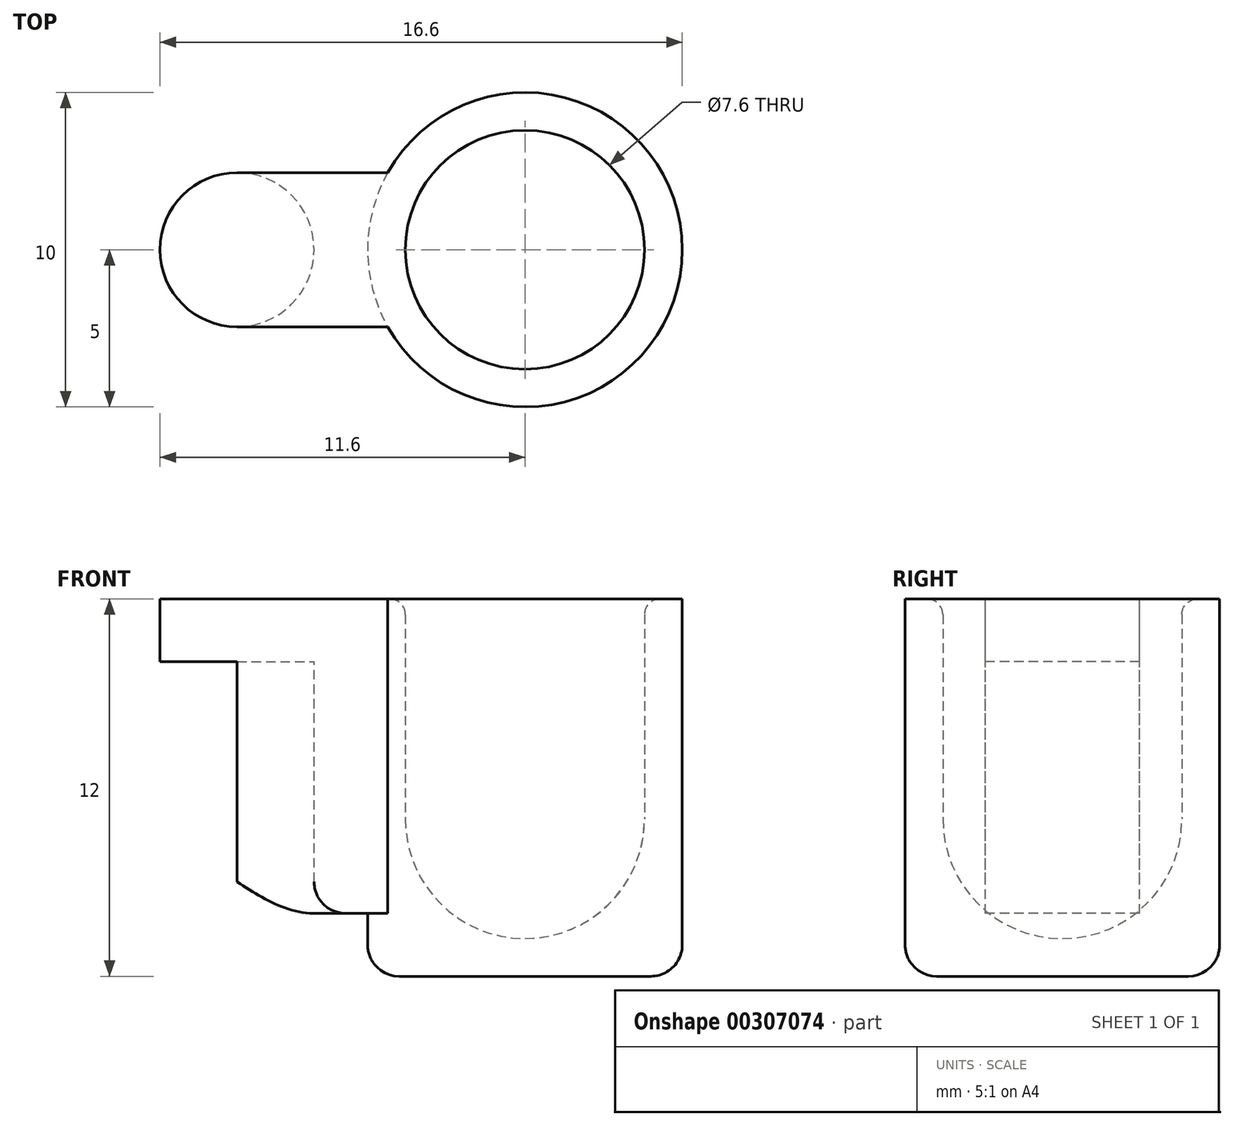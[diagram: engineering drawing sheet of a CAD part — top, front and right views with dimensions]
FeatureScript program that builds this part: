
annotation { "Feature Type Name" : "Feature", "Feature Type Description" : "" }
export const myFeature = defineFeature(function(context is Context, id is Id, definition is map)
    precondition{}
    {
        {
            var Q0;
            Q0=qCreatedBy(makeId("Top.planeOp"),FACE);
            var sketch = newSketch(context, id + "F0", { "sketchPlane" : qUnion([Q0])});
            skCircle(sketch, "E0", {"center": v(0, 0) * mm, "radius": 5 * mm});
            skSolve(sketch);
        }
        {
            var Q0;
            Q0=makeQuery(id+"F0.imprint","IMPRINT",FACE,{"disambiguationData":[TD([[makeQuery(id+"F0.imprint","IMPRINT",EDGE,{"derivedFrom":sQuery(id+"F0.wireOp",EDGE,"E0")}),1.0]])]});
            extrude(context, id + "F1", {"entities" : qUnion([Q0]), "depth" : 12 * mm});
        }
        {
            var Q0;
            Q0=makeQuery(id+"F1.opExtrude","CAP_FACE",FACE,{"disambiguationData":[OSD([sQuery(id+"F0.wireOp",EDGE,"E0")])],"isStart":false});
            shell(context, id + "F2", {"entities" : qUnion([Q0]), "thickness" : 1.2 * mm});
        }
        {
            var Q0;
            Q0=makeQuery(id+"F1.opExtrude","CAP_FACE",FACE,{"disambiguationData":[OSD([sQuery(id+"F0.wireOp",EDGE,"E0")])],"isStart":true});
            var sketch = newSketch(context, id + "F3", { "sketchPlane" : qUnion([Q0])});
            skCircle(sketch, "E1", {"center": v(0, 0) * mm, "radius": 3.5 * mm});
            skSolve(sketch);
        }
        {
            var Q0;
            Q0=makeQuery(id+"F1.opExtrude","CAP_FACE",FACE,{"disambiguationData":[OSD([sQuery(id+"F0.wireOp",EDGE,"E0")])],"isStart":false});
            var sketch = newSketch(context, id + "F4", { "sketchPlane" : qUnion([Q0])});
            skArc(sketch, "E2", {"start": v(-9.15, 2.45) * mm, "mid": v(-11.6, 0) * mm, "end": v(-9.15, -2.45) * mm});
            skLineSegment(sketch, "E3", {"start": v(-9.15, 0) * mm, "end": v(0, 0) * mm, "construction": true});
            skLineSegment(sketch, "E4", {"start": v(-9.15, 2.45) * mm, "end": v(-4.36, 2.45) * mm});
            skLineSegment(sketch, "E5.MirrorCS", {"start": v(-9.15, -2.45) * mm, "end": v(-4.36, -2.45) * mm});
            skArc(sketch, "E6.0", {"start": v(-4.36, 2.45) * mm, "mid": v(-5, 0) * mm, "end": v(-4.36, -2.45) * mm});
            skSolve(sketch);
        }
        {
            var Q0;
            Q0=makeQuery(id+"F4.imprint","IMPRINT",FACE,{"disambiguationData":[TD([[makeQuery(id+"F4.imprint","IMPRINT",EDGE,{"derivedFrom":sQuery(id+"F4.wireOp",EDGE,"E2")}),1.0]])]});
            extrude(context, id + "F5", {"entities" : qUnion([Q0]), "operationType" : NewBodyOperationType.ADD, "oppositeDirection" : true, "depth" : 2 * mm});
        }
        {
            var Q0;
            Q0=makeQuery(id+"F5.opExtrude","CAP_FACE",FACE,{"disambiguationData":[OSD([sQuery(id+"F4.wireOp",EDGE,"E2"),sQuery(id+"F4.wireOp",EDGE,"E4"),sQuery(id+"F4.wireOp",EDGE,"E5.MirrorCS"),sQuery(id+"F4.wireOp",EDGE,"E6.0")])],"isStart":false});
            var sketch = newSketch(context, id + "F6", { "sketchPlane" : qUnion([Q0])});
            skCircle(sketch, "E7", {"center": v(-9.15, 0) * mm, "radius": 2.45 * mm});
            skSolve(sketch);
        }
        {
            var Q0;
            {var subQ0=sQuery(id+"F6.wireOp",EDGE,"E7");Q0=makeQuery(id+"F6.imprint","IMPRINT",FACE,{"disambiguationData":[TD([[makeQuery(id+"F6.imprint","IMPRINT",EDGE,{"disambiguationData":[OD(0.0)],"derivedFrom":subQ0}),-1.0]])]});}
            extrude(context, id + "F7", {"entities" : qUnion([Q0]), "operationType" : NewBodyOperationType.ADD, "depth" : 8 * mm});
        }
        {
            var Q0;
            Q0=makeQuery(id+"F1.opExtrude","CAP_EDGE",EDGE,{"disambiguationData":[OSD([sQuery(id+"F0.wireOp",EDGE,"E0")])],"isStart":true});
            var Q1;
            Q1=makeQuery(id+"F7.opExtrude","CAP_EDGE",EDGE,{"disambiguationData":[OSD([sQuery(id+"F6.wireOp",EDGE,"E7")])],"isStart":false});
            fillet(context, id + "F8", {"entities" : qUnion([Q0, Q1]), "radius" : 1 * mm, "tangentPropagation" : true, "allowEdgeOverflow" : false});
        }
        {
            var Q0;
            {var subQ0=sQuery(id+"F0.wireOp",EDGE,"E0");Q0=makeQuery(id+"F2.opShell","OFFSET_EDGE",EDGE,{"disambiguationData":[OSD([subQ0]),TDD([makeQuery(id+"F1.opExtrude","CAP_EDGE",EDGE,{"disambiguationData":[OSD([subQ0])],"isStart":false})])]});}
            fillet(context, id + "F9", {"entities" : qUnion([Q0]), "radius" : 0.5 * mm, "tangentPropagation" : true, "allowEdgeOverflow" : false});
        }
        {
            var Q0;
            {var subQ0=sQuery(id+"F0.wireOp",EDGE,"E0");Q0=makeQuery(id+"F2.opShell","OFFSET_EDGE",EDGE,{"disambiguationData":[OSD([subQ0]),TDD([makeQuery(id+"F1.opExtrude","CAP_EDGE",EDGE,{"disambiguationData":[OSD([subQ0])],"isStart":true})])]});}
            fillet(context, id + "F10", {"entities" : qUnion([Q0]), "radius" : (7.6 / 2) * mm, "tangentPropagation" : true, "allowEdgeOverflow" : false});
        }
    });
